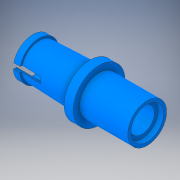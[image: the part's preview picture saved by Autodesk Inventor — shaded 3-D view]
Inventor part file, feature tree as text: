
AUTODESK INVENTOR PART (.ipt)
format: ipt  version: 2017 (Build 210142000, 142)  size: 196,096 bytes
history: native  units: in
note: dims shown in document units (in); Inventor stores cm internally (conversion verified against a paired STEP export)
features: sketch x2, revolve x1, plane x1, extrude x1
ambient origin geometry x8: Origin, YZ Plane, XZ Plane, XY Plane, X Axis, Y Axis, Z Axis, Center Point
bodies: Solid1 (feature_tree)
feature tree (5):
  revolve  "Revolution1"  [1 undecoded]
  plane  "Work Plane1"
  extrude  "Extrusion1"  Depth=0.05in
  sketch  "Sketch1"  dims[d0=0.88in d4=0.025in]
  sketch  "Sketch2"  dims[d7=0.03in d11=0.05in d15=0.33in d17=0.03in d18=0.05in d19=0.015in d21=90.0deg d22=0.04in d23=0.37in d24=0.37in d25=0.44in d26=0.63in d27=0.075in d28=0.125in d29=0.325in d30=0.5321in d31=0.0254in d32=0.0643in d33=0.0in d34=0.275in d35=0.2777in d36=0.88in d37=0.88in d38=90.0deg d44=0.2in d45=0.04in d46=0.1163in d47=0.25in d48=0.0in]
note: 1 required parameter value undecoded (feature->parameter linkage not recoverable at this tier; creation-order binding heuristic only, values carry confidence <= 0.55)
